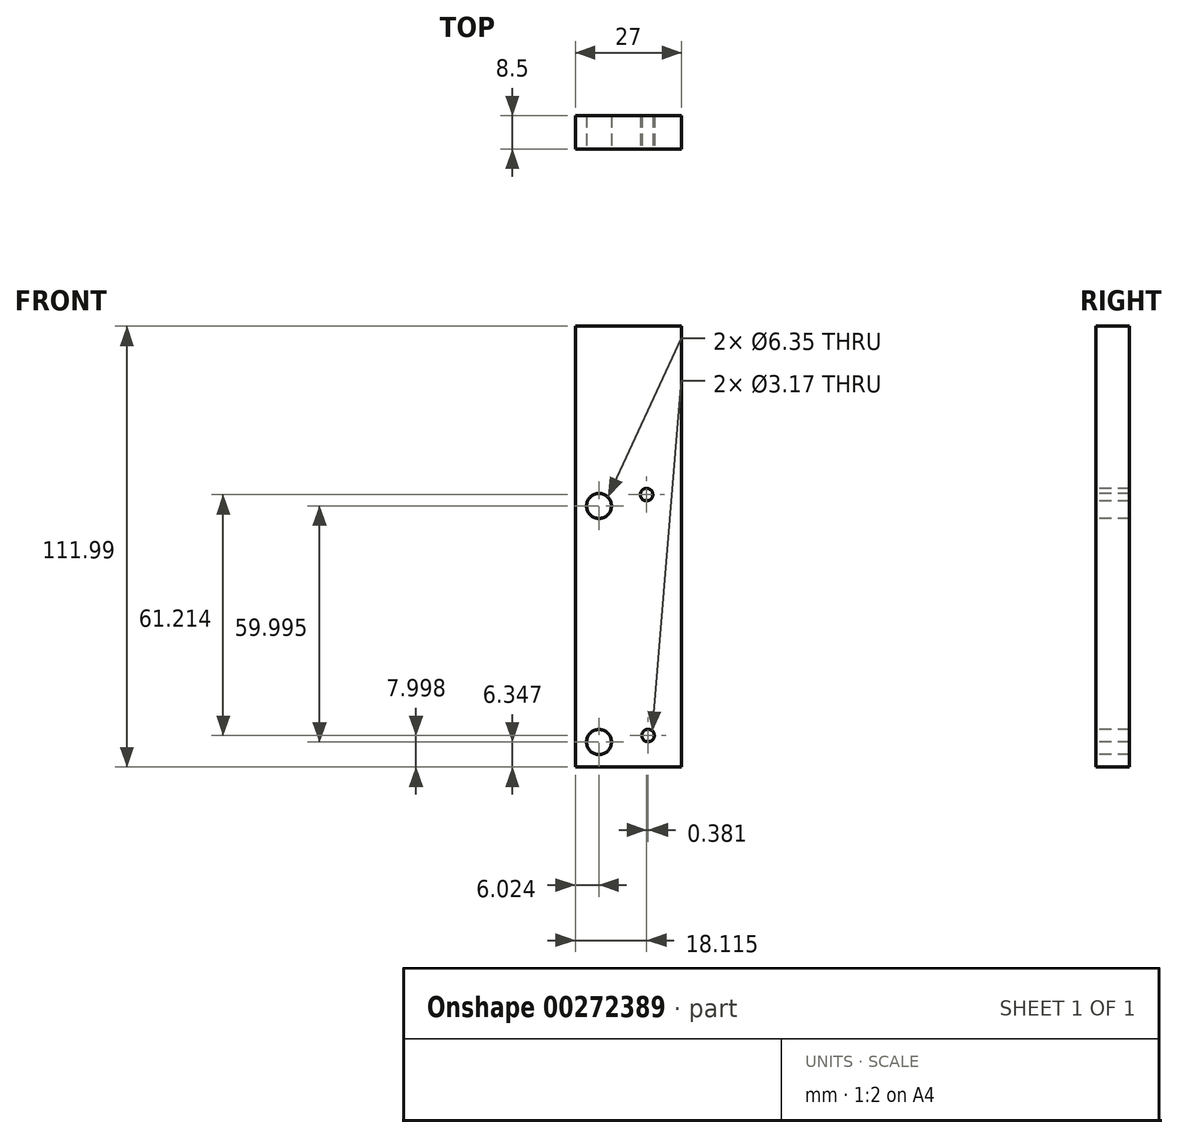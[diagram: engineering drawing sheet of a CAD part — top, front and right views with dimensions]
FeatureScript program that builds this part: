
annotation { "Feature Type Name" : "Feature", "Feature Type Description" : "" }
export const myFeature = defineFeature(function(context is Context, id is Id, definition is map)
    precondition{}
    {
        {
            var Q0;
            Q0=qCreatedBy(makeId("Front.planeOp"),FACE);
            var sketch = newSketch(context, id + "F0", { "sketchPlane" : qUnion([Q0])});
            skLineSegment(sketch, "E0.bottom", {"start": v(-34.77, 31.4) * mm, "end": v(-61.77, 31.4) * mm});
            skLineSegment(sketch, "E0.top", {"start": v(-34.77, -80.6) * mm, "end": v(-61.77, -80.6) * mm});
            skLineSegment(sketch, "E0.left", {"start": v(-34.77, 31.4) * mm, "end": v(-34.77, -80.6) * mm});
            skLineSegment(sketch, "E0.right", {"start": v(-61.77, 31.4) * mm, "end": v(-61.77, -80.6) * mm});
            skCircle(sketch, "E1", {"center": v(-55.75, -14.25) * mm, "radius": 3.17 * mm});
            skPoint(sketch, "E1.first.point", {"position": v(-55.75, -11.07) * mm});
            skPoint(sketch, "E1.second.point", {"position": v(-52.57, -14.25) * mm});
            skPoint(sketch, "E1.third.point", {"position": v(-57.93, -16.55) * mm});
            skCircle(sketch, "E2", {"center": v(-43.66, -11.38) * mm, "radius": 1.59 * mm});
            skPoint(sketch, "E2.first.point", {"position": v(-43.66, -12.97) * mm});
            skPoint(sketch, "E2.second.point", {"position": v(-42.07, -11.38) * mm});
            skPoint(sketch, "E2.third.point", {"position": v(-45.24, -11.38) * mm});
            skCircle(sketch, "E3", {"center": v(-55.75, -74.24) * mm, "radius": 3.18 * mm});
            skPoint(sketch, "E3.first.point", {"position": v(-54.46, -71.34) * mm});
            skPoint(sketch, "E3.second.point", {"position": v(-52.57, -74.24) * mm});
            skPoint(sketch, "E3.third.point", {"position": v(-57.93, -76.55) * mm});
            skCircle(sketch, "E4", {"center": v(-43.27, -72.6) * mm, "radius": 1.59 * mm});
            skPoint(sketch, "E4.first.point", {"position": v(-41.69, -72.6) * mm});
            skPoint(sketch, "E4.second.point", {"position": v(-44.32, -73.79) * mm});
            skPoint(sketch, "E4.third.point", {"position": v(-44.03, -71.2) * mm});
            skSolve(sketch);
        }
        {
            var Q0;
            Q0=makeQuery(id+"F0.imprint","IMPRINT",FACE,{"disambiguationData":[TD([[makeQuery(id+"F0.imprint","IMPRINT",EDGE,{"derivedFrom":sQuery(id+"F0.wireOp",EDGE,"E0.bottom")}),1.0]])]});
            extrude(context, id + "F1", {"entities" : qUnion([Q0]), "oppositeDirection" : true, "depth" : 8.5 * mm});
        }
    });
